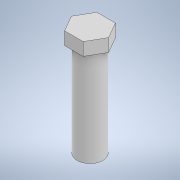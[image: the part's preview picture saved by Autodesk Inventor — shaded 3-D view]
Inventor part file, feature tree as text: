
AUTODESK INVENTOR PART (.ipt)
format: ipt  version: 2020.2 (Build 242310000, 310)  size: 103,424 bytes
history: native  units: in
note: dims shown in document units (in); Inventor stores cm internally (conversion verified against a paired STEP export)
features: extrude x2, sketch x2
ambient origin geometry x8: Origin, YZ Plane, XZ Plane, XY Plane, X Axis, Y Axis, Z Axis, Center Point
bodies: Solid1 (feature_tree)
feature tree (4):
  extrude  "Extrusion1"  Depth=0.5906in TaperAngle=0.0deg
  extrude  "Extrusion2"  Depth=0.0787in TaperAngle=0.0deg
  sketch  "Sketch1"  dims[d0=0.1575in d1=0.5906in d2=0.0in]
  sketch  "Sketch2"  dims[d3=0.1969in d4=0.0787in d5=0.0in]
